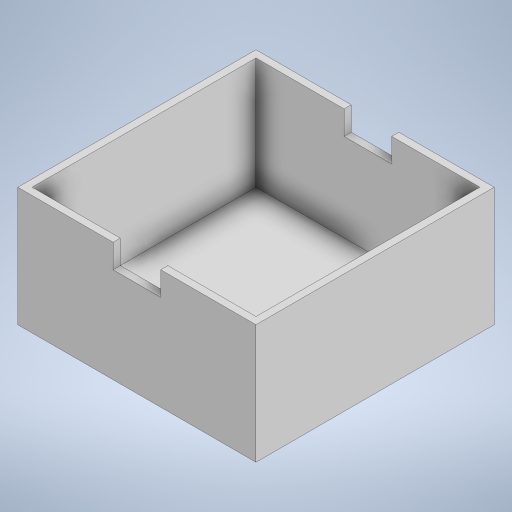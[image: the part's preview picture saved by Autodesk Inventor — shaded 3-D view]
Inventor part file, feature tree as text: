
AUTODESK INVENTOR PART (.ipt)
format: ipt  version: 2024 (Build 280153000, 153)  size: 220,160 bytes
history: native  units: mm
features: extrude x2, sketch x2
ambient origin geometry x8: Origin, YZ Plane, XZ Plane, XY Plane, X Axis, Y Axis, Z Axis, Center Point
bodies: Body1 (feature_tree)
feature tree (4):
  extrude  "Extrusion3"  Depth=50.0mm
  extrude  "Extrusion4"  Depth=10.0mm
  sketch  "Sketch1"  dims[d0=100.0mm d1=50.0mm]
  sketch  "Sketch3"  dims[d2=40.0mm d3=10.0mm d4=20.0mm d5=10.0mm d6=40.0mm d7=50.0mm d34=50.0mm d35=50.0mm d36=100.0mm d37=0.0mm d38=3.0mm d39=47.0mm d40=0.0mm]
